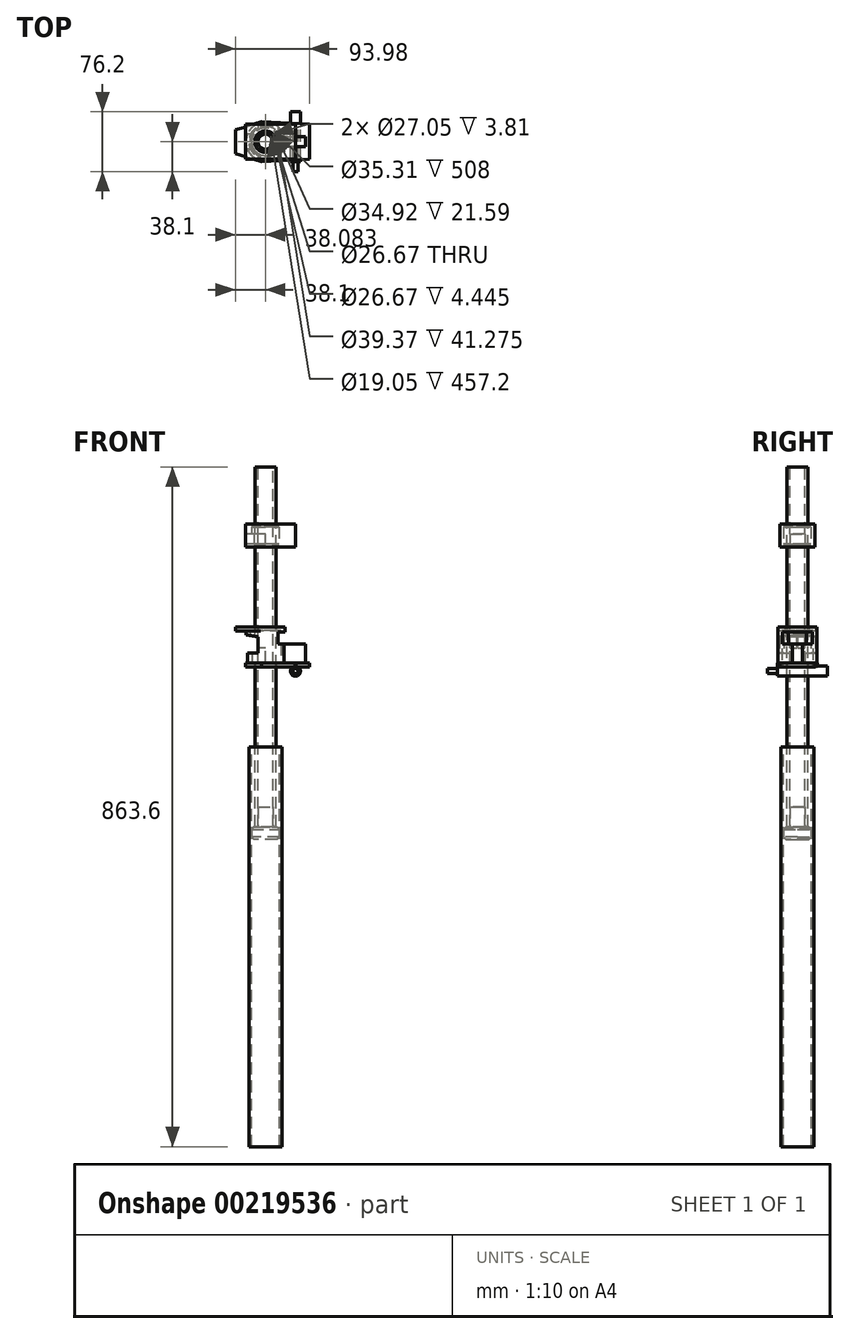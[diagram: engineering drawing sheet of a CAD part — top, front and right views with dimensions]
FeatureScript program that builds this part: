
annotation { "Feature Type Name" : "Feature", "Feature Type Description" : "" }
export const myFeature = defineFeature(function(context is Context, id is Id, definition is map)
    precondition{}
    {
        {
            var Q0;
            Q0=qCreatedBy(makeId("Top.planeOp"),FACE);
            var sketch = newSketch(context, id + "F0", { "sketchPlane" : qUnion([Q0])});
            skLineSegment(sketch, "E0", {"start": v(0, 19.05) * mm, "end": v(0, -19.05) * mm});
            skLineSegment(sketch, "E1", {"start": v(0, -19.05) * mm, "end": v(20.32, -25.4) * mm});
            skLineSegment(sketch, "E2", {"start": v(20.32, -25.4) * mm, "end": v(81.28, -22.23) * mm});
            skLineSegment(sketch, "E3", {"start": v(81.28, -22.23) * mm, "end": v(81.28, 22.23) * mm});
            skLineSegment(sketch, "E4", {"start": v(81.28, 22.23) * mm, "end": v(20.32, 25.4) * mm});
            skLineSegment(sketch, "E5", {"start": v(20.32, 25.4) * mm, "end": v(0, 19.05) * mm});
            skLineSegment(sketch, "E6", {"start": v(0, 0) * mm, "end": v(81.28, 0) * mm, "construction": true});
            skCircle(sketch, "E7", {"center": v(25.4, 0) * mm, "radius": 13.34 * mm});
            skCircle(sketch, "E8", {"center": v(25.4, 0) * mm, "radius": 24.77 * mm});
            skLineSegment(sketch, "E9", {"start": v(49.34, 6.35) * mm, "end": v(76.2, 6.35) * mm});
            skLineSegment(sketch, "E10", {"start": v(76.2, 6.35) * mm, "end": v(76.2, -6.35) * mm});
            skLineSegment(sketch, "E11", {"start": v(76.2, -6.35) * mm, "end": v(49.34, -6.35) * mm});
            skSolve(sketch);
        }
        {
            var Q0;
            Q0=makeQuery(id+"F0.imprint","IMPRINT",FACE,{"disambiguationData":[TD([[makeQuery(id+"F0.imprint","IMPRINT",EDGE,{"derivedFrom":sQuery(id+"F0.wireOp",EDGE,"E0")}),1.0]])]});
            var Q1;
            {var subQ0=sQuery(id+"F0.wireOp",EDGE,"E9");Q1=makeQuery(id+"F0.imprint","IMPRINT",FACE,{"disambiguationData":[TD([[makeQuery(id+"F0.imprint","IMPRINT",EDGE,{"derivedFrom":subQ0}),-1.0]])]});}
            var Q2;
            Q2=makeQuery(id+"F0.imprint","IMPRINT",FACE,{"disambiguationData":[TD([[makeQuery(id+"F0.imprint","IMPRINT",EDGE,{"derivedFrom":sQuery(id+"F0.wireOp",EDGE,"E7")}),-1.0]])]});
            extrude(context, id + "F1", {"entities" : qUnion([Q0, Q1, Q2]), "depth" : 5.08 * mm});
        }
        {
            var Q0;
            Q0=makeQuery(id+"F0.imprint","IMPRINT",FACE,{"disambiguationData":[TD([[makeQuery(id+"F0.imprint","IMPRINT",EDGE,{"derivedFrom":sQuery(id+"F0.wireOp",EDGE,"E7")}),-1.0]])]});
            extrude(context, id + "F2", {"entities" : qUnion([Q0]), "operationType" : NewBodyOperationType.ADD, "depth" : 50.8 * mm});
        }
        {
            var Q0;
            {var subQ0=sQuery(id+"F0.wireOp",EDGE,"E9");Q0=makeQuery(id+"F0.imprint","IMPRINT",FACE,{"disambiguationData":[TD([[makeQuery(id+"F0.imprint","IMPRINT",EDGE,{"derivedFrom":subQ0}),-1.0]])]});}
            extrude(context, id + "F3", {"entities" : qUnion([Q0]), "operationType" : NewBodyOperationType.ADD, "depth" : 29.2 * mm});
        }
        {
            var Q0;
            Q0=makeQuery(id+"F2.opExtrude","CAP_FACE",FACE,{"disambiguationData":[OSD([sQuery(id+"F0.wireOp",EDGE,"E7"),sQuery(id+"F0.wireOp",EDGE,"E8")])],"isStart":false});
            var sketch = newSketch(context, id + "F4", { "sketchPlane" : qUnion([Q0])});
            skLineSegment(sketch, "E12", {"start": v(21.02, 24.38) * mm, "end": v(-12.7, 15.24) * mm});
            skLineSegment(sketch, "E13", {"start": v(-12.7, 15.24) * mm, "end": v(-12.7, -15.24) * mm});
            skLineSegment(sketch, "E14", {"start": v(-12.7, -15.24) * mm, "end": v(18.86, -23.88) * mm});
            skLineSegment(sketch, "E15", {"start": v(25.4, 0) * mm, "end": v(-12.7, 0) * mm, "construction": true});
            skSolve(sketch);
        }
        {
            var Q0;
            {var subQ0=sQuery(id+"F4.wireOp",EDGE,"E13");Q0=makeQuery(id+"F4.imprint","IMPRINT",FACE,{"disambiguationData":[TD([[makeQuery(id+"F4.imprint","IMPRINT",EDGE,{"derivedFrom":subQ0}),1.0]])]});}
            extrude(context, id + "F5", {"entities" : qUnion([Q0]), "operationType" : NewBodyOperationType.ADD, "oppositeDirection" : true, "depth" : 5.08 * mm});
        }
        {
            var Q0;
            Q0=makeQuery(id+"F1.opExtrude","CAP_FACE",FACE,{"disambiguationData":[OSD([sQuery(id+"F0.wireOp",EDGE,"E0"),sQuery(id+"F0.wireOp",EDGE,"E1"),sQuery(id+"F0.wireOp",EDGE,"E2"),sQuery(id+"F0.wireOp",EDGE,"E3"),sQuery(id+"F0.wireOp",EDGE,"E4"),sQuery(id+"F0.wireOp",EDGE,"E5"),sQuery(id+"F0.wireOp",EDGE,"E7")])],"isStart":false});
            var sketch = newSketch(context, id + "F6", { "sketchPlane" : qUnion([Q0])});
            skCircle(sketch, "E16", {"center": v(25.4, 0) * mm, "radius": 19.69 * mm});
            skSolve(sketch);
        }
        {
            var Q0;
            Q0 = qSketchRegion(id + "F6", true);
            extrude(context, id + "F7", {"entities" : qUnion([Q0]), "operationType" : NewBodyOperationType.REMOVE, "depth" : 41.27 * mm});
        }
        {
            var Q0;
            Q0=qCreatedBy(makeId("Top.planeOp"),FACE);
            cPlane(context, id + "F8", {"entities" : qUnion([Q0]), "cplaneType" : CPlaneType.OFFSET, "offset" : 254 * mm, "width" : 152.4 * mm, "height" : 152.4 * mm});
        }
        {
            var Q0;
            Q0=qCreatedBy(id+"F8.planeOp",FACE);
            var sketch = newSketch(context, id + "F9", { "sketchPlane" : qUnion([Q0])});
            skCircle(sketch, "E17", {"center": v(25.38, 0) * mm, "radius": 13.34 * mm});
            skCircle(sketch, "E18", {"center": v(25.38, 0) * mm, "radius": 9.53 * mm});
            skSolve(sketch);
        }
        {
            var Q0;
            Q0 = qSketchRegion(id + "F9", true);
            extrude(context, id + "F10", {"entities" : qUnion([Q0]), "oppositeDirection" : true, "depth" : 457.2 * mm});
        }
        {
            var Q0;
            Q0=qCreatedBy(makeId("Front.planeOp"),FACE);
            cPlane(context, id + "F11", {"entities" : qUnion([Q0]), "cplaneType" : CPlaneType.OFFSET, "offset" : 25.4 * mm, "width" : 152.4 * mm, "height" : 152.4 * mm});
        }
        {
            var Q0;
            Q0=qCreatedBy(id+"F11.planeOp",FACE);
            var sketch = newSketch(context, id + "F12", { "sketchPlane" : qUnion([Q0])});
            skLineSegment(sketch, "E19", {"start": v(-14.6, 17.78) * mm, "end": v(15.88, 17.78) * mm});
            skLineSegment(sketch, "E20", {"start": v(15.88, 17.78) * mm, "end": v(15.88, 38.1) * mm});
            skLineSegment(sketch, "E21", {"start": v(15.88, 38.1) * mm, "end": v(-14.6, 43.18) * mm});
            skLineSegment(sketch, "E22", {"start": v(-14.6, 43.18) * mm, "end": v(-14.6, 17.78) * mm});
            skLineSegment(sketch, "E23", {"start": v(68.14, 44.45) * mm, "end": v(41.28, 44.45) * mm});
            skLineSegment(sketch, "E24", {"start": v(41.28, 44.45) * mm, "end": v(41.28, 29.2) * mm});
            skLineSegment(sketch, "E25", {"start": v(41.28, 29.2) * mm, "end": v(68.14, 29.21) * mm});
            skLineSegment(sketch, "E26", {"start": v(68.14, 29.21) * mm, "end": v(68.14, 44.45) * mm});
            skSolve(sketch);
        }
        {
            var Q0;
            Q0 = qSketchRegion(id + "F12", true);
            extrude(context, id + "F13", {"entities" : qUnion([Q0]), "operationType" : NewBodyOperationType.REMOVE, "endBound" : BoundingType.THROUGH_ALL, "oppositeDirection" : true, "depth" : 25.4 * mm});
        }
        {
            var Q0;
            Q0=qCreatedBy(makeId("Front.planeOp"),FACE);
            var sketch = newSketch(context, id + "F14", { "sketchPlane" : qUnion([Q0])});
            skCircle(sketch, "E27", {"center": v(63.5, -5.59) * mm, "radius": 6.35 * mm});
            skSolve(sketch);
        }
        {
            var Q0;
            Q0 = qSketchRegion(id + "F14", true);
            extrude(context, id + "F15", {"entities" : qUnion([Q0]), "operationType" : NewBodyOperationType.ADD, "depth" : 76.2 * mm, "symmetric" : true});
        }
        {
            var Q0;
            Q0=makeQuery(id+"F15.opExtrude","CAP_FACE",FACE,{"disambiguationData":[OSD([sQuery(id+"F14.wireOp",EDGE,"E27")])],"isStart":false});
            var sketch = newSketch(context, id + "F16", { "sketchPlane" : qUnion([Q0])});
            skCircle(sketch, "E28", {"center": v(63.5, -5.59) * mm, "radius": 3.18 * mm});
            skCircle(sketch, "E29", {"center": v(63.5, -5.59) * mm, "radius": 7.93 * mm});
            skSolve(sketch);
        }
        {
            var Q0;
            Q0 = qSketchRegion(id + "F16", true);
            extrude(context, id + "F17", {"entities" : qUnion([Q0]), "operationType" : NewBodyOperationType.REMOVE, "oppositeDirection" : true, "depth" : 12.7 * mm});
        }
        {
            var Q0;
            Q0=qCreatedBy(makeId("Right.planeOp"),FACE);
            var sketch = newSketch(context, id + "F18", { "sketchPlane" : qUnion([Q0])});
            skLineSegment(sketch, "E30.bottom", {"start": v(9.52, 24.13) * mm, "end": v(-9.52, 24.13) * mm});
            skLineSegment(sketch, "E30.top", {"start": v(9.53, 5.08) * mm, "end": v(-9.53, 5.08) * mm});
            skLineSegment(sketch, "E30.left", {"start": v(9.52, 24.13) * mm, "end": v(9.53, 5.08) * mm});
            skLineSegment(sketch, "E30.right", {"start": v(-9.52, 24.13) * mm, "end": v(-9.53, 5.08) * mm});
            skLineSegment(sketch, "E31", {"start": v(0, 0) * mm, "end": v(0, 24.13) * mm, "construction": true});
            skSolve(sketch);
        }
        {
            var Q0;
            Q0 = qSketchRegion(id + "F18", true);
            extrude(context, id + "F19", {"entities" : qUnion([Q0]), "operationType" : NewBodyOperationType.REMOVE, "depth" : 25.4 * mm});
        }
        {
            var Q0;
            Q0=makeQuery(id+"F10.opExtrude","CAP_FACE",FACE,{"disambiguationData":[OSD([sQuery(id+"F9.wireOp",EDGE,"E17"),sQuery(id+"F9.wireOp",EDGE,"E18")])],"isStart":false});
            cPlane(context, id + "F20", {"entities" : qUnion([Q0]), "cplaneType" : CPlaneType.OFFSET, "offset" : 101.6 * mm, "oppositeDirection" : true, "width" : 152.4 * mm, "height" : 152.4 * mm});
        }
        {
            var Q0;
            Q0=qCreatedBy(id+"F20.planeOp",FACE);
            var sketch = newSketch(context, id + "F21", { "sketchPlane" : qUnion([Q0])});
            skCircle(sketch, "E32", {"center": v(25.38, 0) * mm, "radius": 17.65 * mm});
            skCircle(sketch, "E33", {"center": v(25.38, 0) * mm, "radius": 21.08 * mm});
            skSolve(sketch);
        }
        {
            var Q0;
            Q0=makeQuery(id+"F21.imprint","IMPRINT",FACE,{"disambiguationData":[TD([[makeQuery(id+"F21.imprint","IMPRINT",EDGE,{"derivedFrom":sQuery(id+"F21.wireOp",EDGE,"E32")}),-1.0]])]});
            var Q1;
            Q1=sQuery(id+"F21.wireOp",EDGE,"E33");
            var Q2;
            Q2=sQuery(id+"F21.wireOp",EDGE,"E32");
            extrude(context, id + "F22", {"entities" : qUnion([Q0]), "surfaceEntities" : qUnion([Q1, Q2]), "depth" : 508 * mm});
        }
        {
            var Q0;
            Q0=sQuery(id+"F0.wireOp",VERTEX,"E7.center");
            var Q1;
            Q1=qCreatedBy(makeId("Right.planeOp"),FACE);
            cPlane(context, id + "F23", {"entities" : qUnion([Q0, Q1]), "cplaneType" : CPlaneType.PLANE_POINT, "offset" : 25.4 * mm, "width" : 152.4 * mm, "height" : 152.4 * mm});
        }
        {
            var Q0;
            Q0=qCreatedBy(id+"F23.planeOp",FACE);
            var sketch = newSketch(context, id + "F24", { "sketchPlane" : qUnion([Q0])});
            skLineSegment(sketch, "E34", {"start": v(-9.48, -177.8) * mm, "end": v(-9.48, -203.2) * mm});
            skLineSegment(sketch, "E35", {"start": v(-9.48, -203.2) * mm, "end": v(-17.65, -203.2) * mm});
            skLineSegment(sketch, "E36", {"start": v(-17.65, -203.2) * mm, "end": v(-17.65, -219.08) * mm});
            skLineSegment(sketch, "E37", {"start": v(-17.65, -219.08) * mm, "end": v(0, -219.08) * mm});
            skLineSegment(sketch, "E38", {"start": v(0, -219.08) * mm, "end": v(0, -177.8) * mm});
            skLineSegment(sketch, "E39", {"start": v(0, -177.8) * mm, "end": v(-9.48, -177.8) * mm});
            skSolve(sketch);
        }
        {
            var Q0;
            Q0=makeQuery(id+"F24.imprint","IMPRINT",FACE,{"disambiguationData":[TD([[makeQuery(id+"F24.imprint","IMPRINT",EDGE,{"derivedFrom":sQuery(id+"F24.wireOp",EDGE,"E34")}),1.0]])]});
            var Q1;
            Q1=sQuery(id+"F24.wireOp",EDGE,"E38");
            revolve(context, id + "F25", {"entities" : qUnion([Q0]), "axis" : qUnion([Q1]), "revolveType" : RevolveType.FULL});
        }
        {
            var Q0;
            Q0=makeQuery(id+"F25.opRevolve","SWEPT_EDGE",EDGE,{"disambiguationData":[OSD([sQuery(id+"F24.wireOp",EDGE,"E36"),sQuery(id+"F24.wireOp",EDGE,"E37")])]});
            var Q1;
            Q1=makeQuery(id+"F25.opRevolve","SWEPT_EDGE",EDGE,{"disambiguationData":[OSD([sQuery(id+"F24.wireOp",EDGE,"E35"),sQuery(id+"F24.wireOp",EDGE,"E36")])]});
            chamfer(context, id + "F26", {"entities" : qUnion([Q0, Q1]), "width" : 3.17 * mm, "tangentPropagation" : true});
        }
        {
            var Q0;
            Q0=qCreatedBy(makeId("Top.planeOp"),FACE);
            cPlane(context, id + "F27", {"entities" : qUnion([Q0]), "cplaneType" : CPlaneType.OFFSET, "offset" : 152.4 * mm, "width" : 152.4 * mm, "height" : 152.4 * mm});
        }
        {
            var Q0;
            Q0=qCreatedBy(id+"F27.planeOp",FACE);
            var sketch = newSketch(context, id + "F28", { "sketchPlane" : qUnion([Q0])});
            skLineSegment(sketch, "E40.bottom", {"start": v(0, 22.23) * mm, "end": v(63.48, 22.23) * mm});
            skLineSegment(sketch, "E40.top", {"start": v(0, -22.23) * mm, "end": v(63.48, -22.23) * mm});
            skLineSegment(sketch, "E40.left", {"start": v(0, 22.23) * mm, "end": v(0, -22.23) * mm});
            skLineSegment(sketch, "E40.right", {"start": v(63.48, 22.23) * mm, "end": v(63.48, -22.23) * mm});
            skLineSegment(sketch, "E41", {"start": v(0, 0) * mm, "end": v(25.38, 0) * mm, "construction": true});
            skCircle(sketch, "E42", {"center": v(25.38, 0) * mm, "radius": 13.53 * mm});
            skCircle(sketch, "E43", {"center": v(25.38, 0) * mm, "radius": 17.46 * mm});
            skSolve(sketch);
        }
        {
            var Q0;
            Q0=makeQuery(id+"F28.imprint","IMPRINT",FACE,{"disambiguationData":[TD([[makeQuery(id+"F28.imprint","IMPRINT",EDGE,{"derivedFrom":sQuery(id+"F28.wireOp",EDGE,"E42")}),-1.0]])]});
            var Q1;
            Q1=makeQuery(id+"F28.imprint","IMPRINT",FACE,{"disambiguationData":[TD([[makeQuery(id+"F28.imprint","IMPRINT",EDGE,{"derivedFrom":sQuery(id+"F28.wireOp",EDGE,"E40.bottom")}),-1.0]])]});
            extrude(context, id + "F29", {"entities" : qUnion([Q0, Q1]), "depth" : 3.8 * mm});
        }
        {
            var Q0;
            Q0=makeQuery(id+"F28.imprint","IMPRINT",FACE,{"disambiguationData":[TD([[makeQuery(id+"F28.imprint","IMPRINT",EDGE,{"derivedFrom":sQuery(id+"F28.wireOp",EDGE,"E40.bottom")}),-1.0]])]});
            extrude(context, id + "F30", {"entities" : qUnion([Q0]), "operationType" : NewBodyOperationType.ADD, "depth" : 25.4 * mm});
        }
        {
            var Q0;
            Q0=makeQuery(id+"F30.opExtrude","CAP_FACE",FACE,{"disambiguationData":[OSD([sQuery(id+"F28.wireOp",EDGE,"E40.bottom"),sQuery(id+"F28.wireOp",EDGE,"E40.top"),sQuery(id+"F28.wireOp",EDGE,"E40.left"),sQuery(id+"F28.wireOp",EDGE,"E40.right"),sQuery(id+"F28.wireOp",EDGE,"E43")])],"isStart":false});
            var sketch = newSketch(context, id + "F31", { "sketchPlane" : qUnion([Q0])});
            skLineSegment(sketch, "E44.0", {"start": v(0, 22.23) * mm, "end": v(63.48, 22.23) * mm});
            skLineSegment(sketch, "E44.1", {"start": v(0, -22.23) * mm, "end": v(63.48, -22.23) * mm});
            skLineSegment(sketch, "E44.2", {"start": v(0, 22.23) * mm, "end": v(0, -22.23) * mm});
            skLineSegment(sketch, "E44.3", {"start": v(63.48, 22.23) * mm, "end": v(63.48, -22.23) * mm});
            skLineSegment(sketch, "E44.4", {"start": v(0, 0) * mm, "end": v(25.38, 0) * mm});
            skCircle(sketch, "E44.5", {"center": v(25.38, 0) * mm, "radius": 13.53 * mm});
            skCircle(sketch, "E44.6", {"center": v(25.38, 0) * mm, "radius": 17.46 * mm});
            skSolve(sketch);
        }
        {
            var Q0;
            {var subQ3=sQuery(id+"F31.wireOp",EDGE,"E44.0");Q0=makeQuery(id+"F31.imprint","IMPRINT",FACE,{"disambiguationData":[TD([[makeQuery(id+"F31.imprint","IMPRINT",EDGE,{"derivedFrom":subQ3}),-1.0]])]});}
            var Q1;
            Q1=makeQuery(id+"F31.imprint","IMPRINT",FACE,{"disambiguationData":[TD([[makeQuery(id+"F31.imprint","IMPRINT",EDGE,{"derivedFrom":sQuery(id+"F31.wireOp",EDGE,"E44.5")}),-1.0]])]});
            extrude(context, id + "F32", {"entities" : qUnion([Q0, Q1]), "operationType" : NewBodyOperationType.ADD, "depth" : 3.8 * mm});
        }
        {
            var Q0;
            {var subQ0=sQuery(id+"F28.wireOp",EDGE,"E40.left");Q0=makeQuery(id+"FZGjID0iZ52JKwT_6.boolean.opBoolean","MERGE",FACE,{"derivedFrom":[makeQuery(id+"F30.boolean.opBoolean","MERGE",FACE,{"derivedFrom":[makeQuery(id+"F29.opExtrude","SWEPT_FACE",FACE,{"disambiguationData":[OSD([subQ0])]}),makeQuery(id+"F30.opExtrude","SWEPT_FACE",FACE,{"disambiguationData":[OSD([subQ0])]})]}),makeQuery(id+"FZGjID0iZ52JKwT_6.opExtrude","SWEPT_FACE",FACE,{"disambiguationData":[OSD([subQ0])]})]});}
            var sketch = newSketch(context, id + "F33", { "sketchPlane" : qUnion([Q0])});
            skLineSegment(sketch, "E45.bottom", {"start": v(-9.53, 168.9) * mm, "end": v(9.53, 168.9) * mm});
            skLineSegment(sketch, "E45.top", {"start": v(-9.53, 156.21) * mm, "end": v(9.53, 156.21) * mm});
            skLineSegment(sketch, "E45.left", {"start": v(-9.53, 168.9) * mm, "end": v(-9.53, 156.21) * mm});
            skLineSegment(sketch, "E45.right", {"start": v(9.53, 168.9) * mm, "end": v(9.53, 156.21) * mm});
            skLineSegment(sketch, "E46", {"start": v(0, 181.61) * mm, "end": v(0, 152.4) * mm, "construction": true});
            skLineSegment(sketch, "E47", {"start": v(0, 168.9) * mm, "end": v(0, 156.21) * mm, "construction": true});
            skSolve(sketch);
        }
        {
            var Q0;
            Q0 = qSketchRegion(id + "F33", true);
            extrude(context, id + "F34", {"entities" : qUnion([Q0]), "operationType" : NewBodyOperationType.REMOVE, "oppositeDirection" : true, "depth" : 25.4 * mm});
        }
    });
